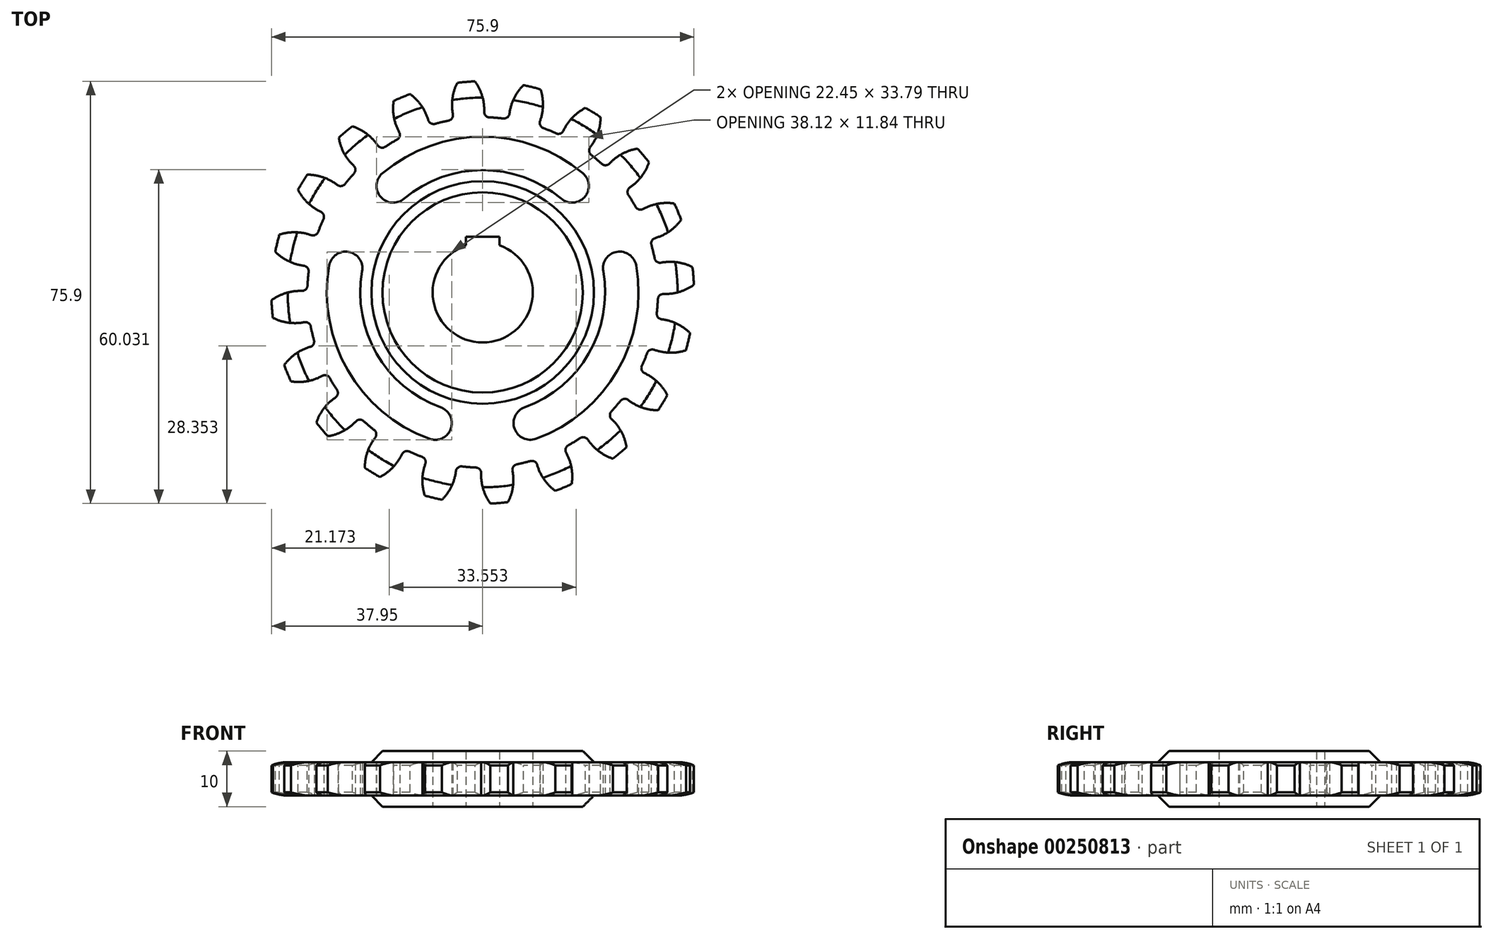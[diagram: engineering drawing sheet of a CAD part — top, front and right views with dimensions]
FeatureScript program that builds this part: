
annotation { "Feature Type Name" : "Feature", "Feature Type Description" : "" }
export const myFeature = defineFeature(function(context is Context, id is Id, definition is map)
    precondition{}
    {
        {
            var Q0;
            Q0=qCreatedBy(makeId("Top.planeOp"),FACE);
            var sketch = newSketch(context, id + "F0", { "sketchPlane" : qUnion([Q0])});
            skArc(sketch, "E0", {"start": v(-3, 8.49) * mm, "mid": v(0, -9) * mm, "end": v(3, 8.49) * mm});
            skCircle(sketch, "E1", {"center": v(0, 0) * mm, "radius": 25 * mm, "construction": true});
            skPoint(sketch, "E2", {"position": v(-46.68, 29.9) * mm});
            skArc(sketch, "E3", {"start": v(-21.67, 3.82) * mm, "mid": v(-24.1, 7.3) * mm, "end": v(-27.57, 4.86) * mm});
            skLineSegment(sketch, "E4", {"start": v(0, 0) * mm, "end": v(-24.62, 4.34) * mm, "construction": true});
            skArc(sketch, "E5", {"start": v(-9.58, -26.31) * mm, "mid": v(-5.73, -24.52) * mm, "end": v(-7.52, -20.67) * mm});
            skLineSegment(sketch, "E6", {"start": v(-8.55, -23.5) * mm, "end": v(0, 0) * mm, "construction": true});
            skArc(sketch, "E7", {"start": v(-27.57, 4.86) * mm, "mid": v(-24.25, -14) * mm, "end": v(-9.58, -26.31) * mm});
            skArc(sketch, "E8", {"start": v(-21.67, 3.82) * mm, "mid": v(-19.05, -11) * mm, "end": v(-7.52, -20.67) * mm});
            skArc(sketch, "E9.1.0", {"start": v(7.52, -20.67) * mm, "mid": v(19.05, -11) * mm, "end": v(21.67, 3.82) * mm});
            skArc(sketch, "E9.1.1", {"start": v(7.52, -20.67) * mm, "mid": v(5.73, -24.52) * mm, "end": v(9.58, -26.31) * mm});
            skArc(sketch, "E9.1.2", {"start": v(9.58, -26.31) * mm, "mid": v(24.25, -14) * mm, "end": v(27.57, 4.86) * mm});
            skArc(sketch, "E9.1.3", {"start": v(27.57, 4.86) * mm, "mid": v(24.1, 7.3) * mm, "end": v(21.67, 3.82) * mm});
            skArc(sketch, "E9.2.0", {"start": v(14.14, 16.85) * mm, "mid": v(0, 22) * mm, "end": v(-14.14, 16.85) * mm});
            skArc(sketch, "E9.2.1", {"start": v(14.14, 16.85) * mm, "mid": v(18.37, 17.22) * mm, "end": v(18, 21.45) * mm});
            skArc(sketch, "E9.2.2", {"start": v(18, 21.45) * mm, "mid": v(0, 28) * mm, "end": v(-18, 21.45) * mm});
            skLineSegment(sketch, "E10", {"start": v(-3, 8.49) * mm, "end": v(-3, 10) * mm});
            skLineSegment(sketch, "E11", {"start": v(-3, 10) * mm, "end": v(3, 10) * mm});
            skLineSegment(sketch, "E12", {"start": v(3, 10) * mm, "end": v(3, 8.49) * mm});
            skArc(sketch, "E13", {"start": v(-18, 21.45) * mm, "mid": v(-18.37, 17.22) * mm, "end": v(-14.14, 16.85) * mm});
            skArc(sketch, "E14", {"start": v(-1.4, 37.97) * mm, "mid": v(-2.98, 37.88) * mm, "end": v(-4.55, 37.73) * mm});
            skArc(sketch, "E15", {"start": v(-28.6, 13.2) * mm, "mid": v(-29.1, 12.05) * mm, "end": v(-29.55, 10.9) * mm});
            skLineSegment(sketch, "E16", {"start": v(0, 0) * mm, "end": v(0, 47.52) * mm, "construction": true});
            skArc(sketch, "E17", {"start": v(0.27, 32.5) * mm, "mid": v(-0.1, 35.38) * mm, "end": v(-1.4, 37.97) * mm});
            skLineSegment(sketch, "E18", {"start": v(0, 0) * mm, "end": v(-2.98, 37.88) * mm, "construction": true});
            skArc(sketch, "E19.MirrorCS", {"start": v(-5.36, 32.07) * mm, "mid": v(-5.43, 34.96) * mm, "end": v(-4.55, 37.73) * mm});
            skArc(sketch, "E20", {"start": v(-5.48, 34.57) * mm, "mid": v(2.75, -34.9) * mm, "end": v(0, 35) * mm, "construction": true});
            skArc(sketch, "E21", {"start": v(0, 35) * mm, "mid": v(-2.75, 34.9) * mm, "end": v(-5.48, 34.57) * mm, "construction": true});
            skArc(sketch, "E22", {"start": v(-6.14, 30.9) * mm, "mid": v(-5.5, 31.32) * mm, "end": v(-5.36, 32.07) * mm});
            skPoint(sketch, "E23.orphan", {"position": v(-5.1, 31.08) * mm});
            skArc(sketch, "E24.MirrorCS", {"start": v(1.23, 31.48) * mm, "mid": v(0.54, 31.8) * mm, "end": v(0.27, 32.5) * mm});
            skPoint(sketch, "E25.orphan", {"position": v(0.18, 31.5) * mm});
            skArc(sketch, "E26.1.0", {"start": v(3.7, 31.28) * mm, "mid": v(4.44, 31.49) * mm, "end": v(4.82, 32.15) * mm});
            skArc(sketch, "E26.1.1", {"start": v(4.82, 32.15) * mm, "mid": v(5.64, 34.93) * mm, "end": v(7.33, 37.29) * mm});
            skArc(sketch, "E26.1.2", {"start": v(10.4, 36.55) * mm, "mid": v(8.87, 36.95) * mm, "end": v(7.33, 37.29) * mm});
            skArc(sketch, "E26.1.3", {"start": v(10.3, 30.83) * mm, "mid": v(10.83, 33.68) * mm, "end": v(10.4, 36.55) * mm});
            skArc(sketch, "E26.1.4", {"start": v(10.9, 29.55) * mm, "mid": v(10.34, 30.07) * mm, "end": v(10.3, 30.83) * mm});
            skArc(sketch, "E26.2.0", {"start": v(13.2, 28.6) * mm, "mid": v(13.95, 28.57) * mm, "end": v(14.51, 29.1) * mm});
            skArc(sketch, "E26.2.1", {"start": v(14.51, 29.1) * mm, "mid": v(16.16, 31.48) * mm, "end": v(18.5, 33.2) * mm});
            skArc(sketch, "E26.2.2", {"start": v(21.18, 31.55) * mm, "mid": v(19.86, 32.4) * mm, "end": v(18.5, 33.2) * mm});
            skArc(sketch, "E26.2.3", {"start": v(19.33, 26.14) * mm, "mid": v(20.7, 28.69) * mm, "end": v(21.18, 31.55) * mm});
            skArc(sketch, "E26.2.4", {"start": v(19.5, 24.74) * mm, "mid": v(19.13, 25.4) * mm, "end": v(19.33, 26.14) * mm});
            skArc(sketch, "E26.3.0", {"start": v(21.38, 23.13) * mm, "mid": v(22.1, 22.86) * mm, "end": v(22.8, 23.18) * mm});
            skArc(sketch, "E26.3.1", {"start": v(22.8, 23.18) * mm, "mid": v(25.1, 24.94) * mm, "end": v(27.85, 25.86) * mm});
            skArc(sketch, "E26.3.2", {"start": v(29.9, 23.46) * mm, "mid": v(28.9, 24.68) * mm, "end": v(27.85, 25.86) * mm});
            skArc(sketch, "E26.3.3", {"start": v(26.46, 18.89) * mm, "mid": v(28.56, 20.89) * mm, "end": v(29.9, 23.46) * mm});
            skArc(sketch, "E26.3.4", {"start": v(26.19, 17.5) * mm, "mid": v(26.04, 18.25) * mm, "end": v(26.46, 18.89) * mm});
            skArc(sketch, "E26.4.0", {"start": v(27.48, 15.39) * mm, "mid": v(28.08, 14.92) * mm, "end": v(28.84, 15) * mm});
            skArc(sketch, "E26.4.1", {"start": v(28.84, 15) * mm, "mid": v(31.58, 15.97) * mm, "end": v(34.47, 15.98) * mm});
            skArc(sketch, "E26.4.2", {"start": v(35.68, 13.07) * mm, "mid": v(35.1, 14.54) * mm, "end": v(34.47, 15.98) * mm});
            skArc(sketch, "E26.4.3", {"start": v(31, 9.79) * mm, "mid": v(33.62, 11.04) * mm, "end": v(35.68, 13.07) * mm});
            skArc(sketch, "E26.4.4", {"start": v(30.32, 8.55) * mm, "mid": v(30.4, 9.31) * mm, "end": v(31, 9.79) * mm});
            skArc(sketch, "E26.5.0", {"start": v(30.9, 6.14) * mm, "mid": v(31.32, 5.5) * mm, "end": v(32.07, 5.36) * mm});
            skArc(sketch, "E26.5.1", {"start": v(32.07, 5.36) * mm, "mid": v(34.96, 5.43) * mm, "end": v(37.73, 4.55) * mm});
            skArc(sketch, "E26.5.2", {"start": v(37.97, 1.4) * mm, "mid": v(37.88, 2.98) * mm, "end": v(37.73, 4.55) * mm});
            skArc(sketch, "E26.5.3", {"start": v(32.5, -0.27) * mm, "mid": v(35.38, 0.1) * mm, "end": v(37.97, 1.4) * mm});
            skArc(sketch, "E26.5.4", {"start": v(31.48, -1.23) * mm, "mid": v(31.8, -0.54) * mm, "end": v(32.5, -0.27) * mm});
            skArc(sketch, "E26.6.0", {"start": v(31.28, -3.7) * mm, "mid": v(31.49, -4.44) * mm, "end": v(32.15, -4.82) * mm});
            skArc(sketch, "E26.6.1", {"start": v(32.15, -4.82) * mm, "mid": v(34.93, -5.64) * mm, "end": v(37.29, -7.33) * mm});
            skArc(sketch, "E26.6.2", {"start": v(36.55, -10.4) * mm, "mid": v(36.95, -8.87) * mm, "end": v(37.29, -7.33) * mm});
            skArc(sketch, "E26.6.3", {"start": v(30.83, -10.3) * mm, "mid": v(33.68, -10.83) * mm, "end": v(36.55, -10.4) * mm});
            skArc(sketch, "E26.6.4", {"start": v(29.55, -10.9) * mm, "mid": v(30.07, -10.34) * mm, "end": v(30.83, -10.3) * mm});
            skArc(sketch, "E26.7.0", {"start": v(28.6, -13.2) * mm, "mid": v(28.57, -13.95) * mm, "end": v(29.1, -14.51) * mm});
            skArc(sketch, "E26.7.1", {"start": v(29.1, -14.51) * mm, "mid": v(31.48, -16.16) * mm, "end": v(33.2, -18.5) * mm});
            skArc(sketch, "E26.7.2", {"start": v(31.55, -21.18) * mm, "mid": v(32.4, -19.86) * mm, "end": v(33.2, -18.5) * mm});
            skArc(sketch, "E26.7.3", {"start": v(26.14, -19.33) * mm, "mid": v(28.69, -20.7) * mm, "end": v(31.55, -21.18) * mm});
            skArc(sketch, "E26.7.4", {"start": v(24.74, -19.5) * mm, "mid": v(25.4, -19.13) * mm, "end": v(26.14, -19.33) * mm});
            skArc(sketch, "E26.8.0", {"start": v(23.13, -21.38) * mm, "mid": v(22.86, -22.1) * mm, "end": v(23.18, -22.8) * mm});
            skArc(sketch, "E26.8.1", {"start": v(23.18, -22.8) * mm, "mid": v(24.94, -25.1) * mm, "end": v(25.86, -27.85) * mm});
            skArc(sketch, "E26.8.2", {"start": v(23.46, -29.9) * mm, "mid": v(24.68, -28.9) * mm, "end": v(25.86, -27.85) * mm});
            skArc(sketch, "E26.8.3", {"start": v(18.89, -26.46) * mm, "mid": v(20.89, -28.56) * mm, "end": v(23.46, -29.9) * mm});
            skArc(sketch, "E26.8.4", {"start": v(17.5, -26.19) * mm, "mid": v(18.25, -26.04) * mm, "end": v(18.89, -26.46) * mm});
            skArc(sketch, "E26.9.0", {"start": v(15.39, -27.48) * mm, "mid": v(14.92, -28.08) * mm, "end": v(15, -28.84) * mm});
            skArc(sketch, "E26.9.1", {"start": v(15, -28.84) * mm, "mid": v(15.97, -31.58) * mm, "end": v(15.98, -34.47) * mm});
            skArc(sketch, "E26.9.2", {"start": v(13.07, -35.68) * mm, "mid": v(14.54, -35.1) * mm, "end": v(15.98, -34.47) * mm});
            skArc(sketch, "E26.9.3", {"start": v(9.79, -31) * mm, "mid": v(11.04, -33.62) * mm, "end": v(13.07, -35.68) * mm});
            skArc(sketch, "E26.9.4", {"start": v(8.55, -30.32) * mm, "mid": v(9.31, -30.4) * mm, "end": v(9.79, -31) * mm});
            skArc(sketch, "E26.10.0", {"start": v(6.14, -30.9) * mm, "mid": v(5.5, -31.32) * mm, "end": v(5.36, -32.07) * mm});
            skArc(sketch, "E26.10.1", {"start": v(5.36, -32.07) * mm, "mid": v(5.43, -34.96) * mm, "end": v(4.55, -37.73) * mm});
            skArc(sketch, "E26.10.2", {"start": v(1.4, -37.97) * mm, "mid": v(2.98, -37.88) * mm, "end": v(4.55, -37.73) * mm});
            skArc(sketch, "E26.10.3", {"start": v(-0.27, -32.5) * mm, "mid": v(0.1, -35.38) * mm, "end": v(1.4, -37.97) * mm});
            skArc(sketch, "E26.10.4", {"start": v(-1.23, -31.48) * mm, "mid": v(-0.54, -31.8) * mm, "end": v(-0.27, -32.5) * mm});
            skArc(sketch, "E26.11.0", {"start": v(-3.7, -31.28) * mm, "mid": v(-4.44, -31.49) * mm, "end": v(-4.82, -32.15) * mm});
            skArc(sketch, "E26.11.1", {"start": v(-4.82, -32.15) * mm, "mid": v(-5.64, -34.93) * mm, "end": v(-7.33, -37.29) * mm});
            skArc(sketch, "E26.11.2", {"start": v(-10.4, -36.55) * mm, "mid": v(-8.87, -36.95) * mm, "end": v(-7.33, -37.29) * mm});
            skArc(sketch, "E26.11.3", {"start": v(-10.3, -30.83) * mm, "mid": v(-10.83, -33.68) * mm, "end": v(-10.4, -36.55) * mm});
            skArc(sketch, "E26.11.4", {"start": v(-10.9, -29.55) * mm, "mid": v(-10.34, -30.07) * mm, "end": v(-10.3, -30.83) * mm});
            skArc(sketch, "E26.12.0", {"start": v(-13.2, -28.6) * mm, "mid": v(-13.95, -28.57) * mm, "end": v(-14.51, -29.1) * mm});
            skArc(sketch, "E26.12.1", {"start": v(-14.51, -29.1) * mm, "mid": v(-16.16, -31.48) * mm, "end": v(-18.5, -33.2) * mm});
            skArc(sketch, "E26.12.2", {"start": v(-21.18, -31.55) * mm, "mid": v(-19.86, -32.4) * mm, "end": v(-18.5, -33.2) * mm});
            skArc(sketch, "E26.12.3", {"start": v(-19.33, -26.14) * mm, "mid": v(-20.7, -28.69) * mm, "end": v(-21.18, -31.55) * mm});
            skArc(sketch, "E26.12.4", {"start": v(-19.5, -24.74) * mm, "mid": v(-19.13, -25.4) * mm, "end": v(-19.33, -26.14) * mm});
            skArc(sketch, "E26.13.0", {"start": v(-21.38, -23.13) * mm, "mid": v(-22.1, -22.86) * mm, "end": v(-22.8, -23.18) * mm});
            skArc(sketch, "E26.13.1", {"start": v(-22.8, -23.18) * mm, "mid": v(-25.1, -24.94) * mm, "end": v(-27.85, -25.86) * mm});
            skArc(sketch, "E26.13.2", {"start": v(-29.9, -23.46) * mm, "mid": v(-28.9, -24.68) * mm, "end": v(-27.85, -25.86) * mm});
            skArc(sketch, "E26.13.3", {"start": v(-26.46, -18.89) * mm, "mid": v(-28.56, -20.89) * mm, "end": v(-29.9, -23.46) * mm});
            skArc(sketch, "E26.13.4", {"start": v(-26.19, -17.5) * mm, "mid": v(-26.04, -18.25) * mm, "end": v(-26.46, -18.89) * mm});
            skArc(sketch, "E26.14.0", {"start": v(-27.48, -15.39) * mm, "mid": v(-28.08, -14.92) * mm, "end": v(-28.84, -15) * mm});
            skArc(sketch, "E26.14.1", {"start": v(-28.84, -15) * mm, "mid": v(-31.58, -15.97) * mm, "end": v(-34.47, -15.98) * mm});
            skArc(sketch, "E26.14.2", {"start": v(-35.68, -13.07) * mm, "mid": v(-35.1, -14.54) * mm, "end": v(-34.47, -15.98) * mm});
            skArc(sketch, "E26.14.3", {"start": v(-31, -9.79) * mm, "mid": v(-33.62, -11.04) * mm, "end": v(-35.68, -13.07) * mm});
            skArc(sketch, "E26.14.4", {"start": v(-30.32, -8.55) * mm, "mid": v(-30.4, -9.31) * mm, "end": v(-31, -9.79) * mm});
            skArc(sketch, "E26.15.0", {"start": v(-30.9, -6.14) * mm, "mid": v(-31.32, -5.5) * mm, "end": v(-32.07, -5.36) * mm});
            skArc(sketch, "E26.15.1", {"start": v(-32.07, -5.36) * mm, "mid": v(-34.96, -5.43) * mm, "end": v(-37.73, -4.55) * mm});
            skArc(sketch, "E26.15.2", {"start": v(-37.97, -1.4) * mm, "mid": v(-37.88, -2.98) * mm, "end": v(-37.73, -4.55) * mm});
            skArc(sketch, "E26.15.3", {"start": v(-32.5, 0.27) * mm, "mid": v(-35.38, -0.1) * mm, "end": v(-37.97, -1.4) * mm});
            skArc(sketch, "E26.15.4", {"start": v(-31.48, 1.23) * mm, "mid": v(-31.8, 0.54) * mm, "end": v(-32.5, 0.27) * mm});
            skArc(sketch, "E26.16.0", {"start": v(-31.28, 3.7) * mm, "mid": v(-31.49, 4.44) * mm, "end": v(-32.15, 4.82) * mm});
            skArc(sketch, "E26.16.1", {"start": v(-32.15, 4.82) * mm, "mid": v(-34.93, 5.64) * mm, "end": v(-37.29, 7.33) * mm});
            skArc(sketch, "E26.16.2", {"start": v(-36.55, 10.4) * mm, "mid": v(-36.95, 8.87) * mm, "end": v(-37.29, 7.33) * mm});
            skArc(sketch, "E26.16.3", {"start": v(-30.83, 10.3) * mm, "mid": v(-33.68, 10.83) * mm, "end": v(-36.55, 10.4) * mm});
            skArc(sketch, "E26.16.4", {"start": v(-29.55, 10.9) * mm, "mid": v(-30.07, 10.34) * mm, "end": v(-30.83, 10.3) * mm});
            skArc(sketch, "E26.17.0", {"start": v(-28.6, 13.2) * mm, "mid": v(-28.57, 13.95) * mm, "end": v(-29.1, 14.51) * mm});
            skArc(sketch, "E26.17.1", {"start": v(-29.1, 14.51) * mm, "mid": v(-31.48, 16.16) * mm, "end": v(-33.2, 18.5) * mm});
            skArc(sketch, "E26.17.2", {"start": v(-31.55, 21.18) * mm, "mid": v(-32.4, 19.86) * mm, "end": v(-33.2, 18.5) * mm});
            skArc(sketch, "E26.17.3", {"start": v(-26.14, 19.33) * mm, "mid": v(-28.69, 20.7) * mm, "end": v(-31.55, 21.18) * mm});
            skArc(sketch, "E26.17.4", {"start": v(-24.74, 19.5) * mm, "mid": v(-25.4, 19.13) * mm, "end": v(-26.14, 19.33) * mm});
            skArc(sketch, "E26.18.0", {"start": v(-23.13, 21.38) * mm, "mid": v(-22.86, 22.1) * mm, "end": v(-23.18, 22.8) * mm});
            skArc(sketch, "E26.18.1", {"start": v(-23.18, 22.8) * mm, "mid": v(-24.94, 25.1) * mm, "end": v(-25.86, 27.85) * mm});
            skArc(sketch, "E26.18.2", {"start": v(-23.46, 29.9) * mm, "mid": v(-24.68, 28.9) * mm, "end": v(-25.86, 27.85) * mm});
            skArc(sketch, "E26.18.3", {"start": v(-18.89, 26.46) * mm, "mid": v(-20.89, 28.56) * mm, "end": v(-23.46, 29.9) * mm});
            skArc(sketch, "E26.18.4", {"start": v(-17.5, 26.19) * mm, "mid": v(-18.25, 26.04) * mm, "end": v(-18.89, 26.46) * mm});
            skArc(sketch, "E26.19.0", {"start": v(-15.39, 27.48) * mm, "mid": v(-14.92, 28.08) * mm, "end": v(-15, 28.84) * mm});
            skArc(sketch, "E26.19.1", {"start": v(-15, 28.84) * mm, "mid": v(-15.97, 31.58) * mm, "end": v(-15.98, 34.47) * mm});
            skArc(sketch, "E26.19.2", {"start": v(-13.07, 35.68) * mm, "mid": v(-14.54, 35.1) * mm, "end": v(-15.98, 34.47) * mm});
            skArc(sketch, "E26.19.3", {"start": v(-9.79, 31) * mm, "mid": v(-11.04, 33.62) * mm, "end": v(-13.07, 35.68) * mm});
            skArc(sketch, "E26.19.4", {"start": v(-8.55, 30.32) * mm, "mid": v(-9.31, 30.4) * mm, "end": v(-9.79, 31) * mm});
            skLineSegment(sketch, "E26.anchor1", {"start": v(0, 0) * mm, "end": v(-6.14, 30.9) * mm, "construction": true});
            skLineSegment(sketch, "E26.anchor2", {"start": v(0, 0) * mm, "end": v(-15.39, 27.48) * mm, "construction": true});
            skArc(sketch, "E27.trimOffspring", {"start": v(-23.13, 21.38) * mm, "mid": v(-23.95, 20.46) * mm, "end": v(-24.74, 19.5) * mm});
            skArc(sketch, "E28.trimOffspring", {"start": v(-15.39, 27.48) * mm, "mid": v(-16.46, 26.86) * mm, "end": v(-17.5, 26.19) * mm});
            skArc(sketch, "E29.trimOffspring", {"start": v(-6.14, 30.9) * mm, "mid": v(-7.35, 30.63) * mm, "end": v(-8.55, 30.32) * mm});
            skArc(sketch, "E30.trimOffspring", {"start": v(3.7, 31.28) * mm, "mid": v(2.47, 31.4) * mm, "end": v(1.23, 31.48) * mm});
            skArc(sketch, "E31.trimOffspring", {"start": v(13.2, 28.6) * mm, "mid": v(12.05, 29.1) * mm, "end": v(10.9, 29.55) * mm});
            skArc(sketch, "E32.trimOffspring", {"start": v(21.38, 23.13) * mm, "mid": v(20.46, 23.95) * mm, "end": v(19.5, 24.74) * mm});
            skArc(sketch, "E33.trimOffspring", {"start": v(27.48, 15.39) * mm, "mid": v(26.86, 16.46) * mm, "end": v(26.19, 17.5) * mm});
            skArc(sketch, "E34.trimOffspring", {"start": v(30.9, 6.14) * mm, "mid": v(30.63, 7.35) * mm, "end": v(30.32, 8.55) * mm});
            skArc(sketch, "E35.trimOffspring", {"start": v(31.28, -3.7) * mm, "mid": v(31.4, -2.47) * mm, "end": v(31.48, -1.23) * mm});
            skArc(sketch, "E36.trimOffspring", {"start": v(28.6, -13.2) * mm, "mid": v(29.1, -12.05) * mm, "end": v(29.55, -10.9) * mm});
            skArc(sketch, "E37.trimOffspring", {"start": v(23.13, -21.38) * mm, "mid": v(23.95, -20.46) * mm, "end": v(24.74, -19.5) * mm});
            skArc(sketch, "E38.trimOffspring", {"start": v(15.39, -27.48) * mm, "mid": v(16.46, -26.86) * mm, "end": v(17.5, -26.19) * mm});
            skArc(sketch, "E39.trimOffspring", {"start": v(6.14, -30.9) * mm, "mid": v(7.35, -30.63) * mm, "end": v(8.55, -30.32) * mm});
            skArc(sketch, "E40.trimOffspring", {"start": v(-3.7, -31.28) * mm, "mid": v(-2.47, -31.4) * mm, "end": v(-1.23, -31.48) * mm});
            skArc(sketch, "E41.trimOffspring", {"start": v(-13.2, -28.6) * mm, "mid": v(-12.05, -29.1) * mm, "end": v(-10.9, -29.55) * mm});
            skArc(sketch, "E42.trimOffspring", {"start": v(-21.38, -23.13) * mm, "mid": v(-20.46, -23.95) * mm, "end": v(-19.5, -24.74) * mm});
            skArc(sketch, "E43.trimOffspring", {"start": v(-27.48, -15.39) * mm, "mid": v(-26.86, -16.46) * mm, "end": v(-26.19, -17.5) * mm});
            skArc(sketch, "E44.trimOffspring", {"start": v(-30.9, -6.14) * mm, "mid": v(-30.63, -7.35) * mm, "end": v(-30.32, -8.55) * mm});
            skArc(sketch, "E45.trimOffspring", {"start": v(-31.28, 3.7) * mm, "mid": v(-31.4, 2.47) * mm, "end": v(-31.48, 1.23) * mm});
            skSolve(sketch);
        }
        {
            var Q0;
            Q0=makeQuery(id+"F0.imprint","IMPRINT",FACE,{"disambiguationData":[TD([[makeQuery(id+"F0.imprint","IMPRINT",EDGE,{"derivedFrom":sQuery(id+"F0.wireOp",EDGE,"E0")}),-1.0]])]});
            extrude(context, id + "F1", {"entities" : qUnion([Q0]), "depth" : 6 * mm, "offsetDistance" : 25 * mm, "symmetric" : true});
        }
        {
            var Q0;
            Q0=qCreatedBy(makeId("Right.planeOp"),FACE);
            var sketch = newSketch(context, id + "F2", { "sketchPlane" : qUnion([Q0])});
            skLineSegment(sketch, "E46", {"start": v(37.97, 2.44) * mm, "end": v(37.97, -2.43) * mm});
            skLineSegment(sketch, "E47", {"start": v(34.73, 3) * mm, "end": v(34.73, -9.64) * mm, "construction": true});
            skArc(sketch, "E48", {"start": v(37.97, 2.44) * mm, "mid": v(36.38, 2.87) * mm, "end": v(34.73, 3) * mm});
            skArc(sketch, "E49.MirrorCS", {"start": v(37.97, -2.44) * mm, "mid": v(36.38, -2.87) * mm, "end": v(34.73, -3) * mm});
            skLineSegment(sketch, "E50", {"start": v(34.73, 3) * mm, "end": v(34.73, 3.33) * mm});
            skLineSegment(sketch, "E51", {"start": v(34.73, 3.33) * mm, "end": v(39.08, 3.33) * mm});
            skLineSegment(sketch, "E52", {"start": v(39.08, 3.33) * mm, "end": v(39.08, -3.22) * mm});
            skLineSegment(sketch, "E53", {"start": v(39.08, -3.22) * mm, "end": v(34.73, -3.32) * mm});
            skLineSegment(sketch, "E54", {"start": v(34.73, -3.32) * mm, "end": v(34.73, -3) * mm});
            skSolve(sketch);
        }
        {
            var Q0;
            Q0=makeQuery(id+"F2.imprint","IMPRINT",FACE,{"disambiguationData":[TD([[makeQuery(id+"F2.imprint","IMPRINT",EDGE,{"derivedFrom":sQuery(id+"F2.wireOp",EDGE,"E46")}),1.0]])]});
            var Q1;
            Q1=makeQuery(id+"F1.opExtrude","SWEPT_FACE",FACE,{"disambiguationData":[OSD([sQuery(id+"F0.wireOp",EDGE,"E0")])]});
            revolve(context, id + "F3", {"operationType" : NewBodyOperationType.REMOVE, "surfaceOperationType" : NewSurfaceOperationType.NEW, "entities" : qUnion([Q0]), "axis" : qUnion([Q1]), "revolveType" : RevolveType.FULL, "oppositeDirection" : true});
        }
        {
            var Q0;
            Q0=qCreatedBy(makeId("Top.planeOp"),FACE);
            var sketch = newSketch(context, id + "F4", { "sketchPlane" : qUnion([Q0])});
            skCircle(sketch, "E55", {"center": v(0, 0) * mm, "radius": 18 * mm});
            skArc(sketch, "E56", {"start": v(-3, 8.49) * mm, "mid": v(0, -9) * mm, "end": v(3, 8.49) * mm});
            skLineSegment(sketch, "E57", {"start": v(3, 8.49) * mm, "end": v(3, 10) * mm});
            skLineSegment(sketch, "E58", {"start": v(3, 10) * mm, "end": v(-3, 10) * mm});
            skLineSegment(sketch, "E59", {"start": v(-3, 10) * mm, "end": v(-3, 8.49) * mm});
            skSolve(sketch);
        }
        {
            var Q0;
            Q0 = qSketchRegion(id + "F4", true);
            extrude(context, id + "F5", {"entities" : qUnion([Q0]), "operationType" : NewBodyOperationType.ADD, "depth" : 10 * mm, "offsetDistance" : 25 * mm, "symmetric" : true});
        }
        {
            var Q0;
            Q0=makeQuery(id+"F5.boolean.opBoolean","INTERSECT",EDGE,{"derivedFrom":[makeQuery(id+"F1.opExtrude","CAP_FACE",FACE,{"disambiguationData":[OSD([sQuery(id+"F0.wireOp",EDGE,"E0"),sQuery(id+"F0.wireOp",EDGE,"E3"),sQuery(id+"F0.wireOp",EDGE,"E5"),sQuery(id+"F0.wireOp",EDGE,"E7"),sQuery(id+"F0.wireOp",EDGE,"E8"),sQuery(id+"F0.wireOp",EDGE,"E9.1.0"),sQuery(id+"F0.wireOp",EDGE,"E9.1.1"),sQuery(id+"F0.wireOp",EDGE,"E9.1.2"),sQuery(id+"F0.wireOp",EDGE,"E9.1.3"),sQuery(id+"F0.wireOp",EDGE,"E9.2.0"),sQuery(id+"F0.wireOp",EDGE,"E9.2.1"),sQuery(id+"F0.wireOp",EDGE,"E9.2.2"),sQuery(id+"F0.wireOp",EDGE,"E10"),sQuery(id+"F0.wireOp",EDGE,"E11"),sQuery(id+"F0.wireOp",EDGE,"E12"),sQuery(id+"F0.wireOp",EDGE,"E13"),sQuery(id+"F0.wireOp",EDGE,"E14"),sQuery(id+"F0.wireOp",EDGE,"E15"),sQuery(id+"F0.wireOp",EDGE,"E17"),sQuery(id+"F0.wireOp",EDGE,"E19.MirrorCS"),sQuery(id+"F0.wireOp",EDGE,"E22"),sQuery(id+"F0.wireOp",EDGE,"E24.MirrorCS"),sQuery(id+"F0.wireOp",EDGE,"E26.1.0"),sQuery(id+"F0.wireOp",EDGE,"E26.1.1"),sQuery(id+"F0.wireOp",EDGE,"E26.1.2"),sQuery(id+"F0.wireOp",EDGE,"E26.1.3"),sQuery(id+"F0.wireOp",EDGE,"E26.1.4"),sQuery(id+"F0.wireOp",EDGE,"E26.2.0"),sQuery(id+"F0.wireOp",EDGE,"E26.2.1"),sQuery(id+"F0.wireOp",EDGE,"E26.2.2"),sQuery(id+"F0.wireOp",EDGE,"E26.2.3"),sQuery(id+"F0.wireOp",EDGE,"E26.2.4"),sQuery(id+"F0.wireOp",EDGE,"E26.3.0"),sQuery(id+"F0.wireOp",EDGE,"E26.3.1"),sQuery(id+"F0.wireOp",EDGE,"E26.3.2"),sQuery(id+"F0.wireOp",EDGE,"E26.3.3"),sQuery(id+"F0.wireOp",EDGE,"E26.3.4"),sQuery(id+"F0.wireOp",EDGE,"E26.4.0"),sQuery(id+"F0.wireOp",EDGE,"E26.4.1"),sQuery(id+"F0.wireOp",EDGE,"E26.4.2"),sQuery(id+"F0.wireOp",EDGE,"E26.4.3"),sQuery(id+"F0.wireOp",EDGE,"E26.4.4"),sQuery(id+"F0.wireOp",EDGE,"E26.5.0"),sQuery(id+"F0.wireOp",EDGE,"E26.5.1"),sQuery(id+"F0.wireOp",EDGE,"E26.5.2"),sQuery(id+"F0.wireOp",EDGE,"E26.5.3"),sQuery(id+"F0.wireOp",EDGE,"E26.5.4"),sQuery(id+"F0.wireOp",EDGE,"E26.6.0"),sQuery(id+"F0.wireOp",EDGE,"E26.6.1"),sQuery(id+"F0.wireOp",EDGE,"E26.6.2"),sQuery(id+"F0.wireOp",EDGE,"E26.6.3"),sQuery(id+"F0.wireOp",EDGE,"E26.6.4"),sQuery(id+"F0.wireOp",EDGE,"E26.7.0"),sQuery(id+"F0.wireOp",EDGE,"E26.7.1"),sQuery(id+"F0.wireOp",EDGE,"E26.7.2"),sQuery(id+"F0.wireOp",EDGE,"E26.7.3"),sQuery(id+"F0.wireOp",EDGE,"E26.7.4"),sQuery(id+"F0.wireOp",EDGE,"E26.8.0"),sQuery(id+"F0.wireOp",EDGE,"E26.8.1"),sQuery(id+"F0.wireOp",EDGE,"E26.8.2"),sQuery(id+"F0.wireOp",EDGE,"E26.8.3"),sQuery(id+"F0.wireOp",EDGE,"E26.8.4"),sQuery(id+"F0.wireOp",EDGE,"E26.9.0"),sQuery(id+"F0.wireOp",EDGE,"E26.9.1"),sQuery(id+"F0.wireOp",EDGE,"E26.9.2"),sQuery(id+"F0.wireOp",EDGE,"E26.9.3"),sQuery(id+"F0.wireOp",EDGE,"E26.9.4"),sQuery(id+"F0.wireOp",EDGE,"E26.10.0"),sQuery(id+"F0.wireOp",EDGE,"E26.10.1"),sQuery(id+"F0.wireOp",EDGE,"E26.10.2"),sQuery(id+"F0.wireOp",EDGE,"E26.10.3"),sQuery(id+"F0.wireOp",EDGE,"E26.10.4"),sQuery(id+"F0.wireOp",EDGE,"E26.11.0"),sQuery(id+"F0.wireOp",EDGE,"E26.11.1"),sQuery(id+"F0.wireOp",EDGE,"E26.11.2"),sQuery(id+"F0.wireOp",EDGE,"E26.11.3"),sQuery(id+"F0.wireOp",EDGE,"E26.11.4"),sQuery(id+"F0.wireOp",EDGE,"E26.12.0"),sQuery(id+"F0.wireOp",EDGE,"E26.12.1"),sQuery(id+"F0.wireOp",EDGE,"E26.12.2"),sQuery(id+"F0.wireOp",EDGE,"E26.12.3"),sQuery(id+"F0.wireOp",EDGE,"E26.12.4"),sQuery(id+"F0.wireOp",EDGE,"E26.13.0"),sQuery(id+"F0.wireOp",EDGE,"E26.13.1"),sQuery(id+"F0.wireOp",EDGE,"E26.13.2"),sQuery(id+"F0.wireOp",EDGE,"E26.13.3"),sQuery(id+"F0.wireOp",EDGE,"E26.13.4"),sQuery(id+"F0.wireOp",EDGE,"E26.14.0"),sQuery(id+"F0.wireOp",EDGE,"E26.14.1"),sQuery(id+"F0.wireOp",EDGE,"E26.14.2"),sQuery(id+"F0.wireOp",EDGE,"E26.14.3"),sQuery(id+"F0.wireOp",EDGE,"E26.14.4"),sQuery(id+"F0.wireOp",EDGE,"E26.15.0"),sQuery(id+"F0.wireOp",EDGE,"E26.15.1"),sQuery(id+"F0.wireOp",EDGE,"E26.15.2"),sQuery(id+"F0.wireOp",EDGE,"E26.15.3"),sQuery(id+"F0.wireOp",EDGE,"E26.15.4"),sQuery(id+"F0.wireOp",EDGE,"E26.16.0"),sQuery(id+"F0.wireOp",EDGE,"E26.16.1"),sQuery(id+"F0.wireOp",EDGE,"E26.16.2"),sQuery(id+"F0.wireOp",EDGE,"E26.16.3"),sQuery(id+"F0.wireOp",EDGE,"E26.16.4"),sQuery(id+"F0.wireOp",EDGE,"E26.17.0"),sQuery(id+"F0.wireOp",EDGE,"E26.17.1"),sQuery(id+"F0.wireOp",EDGE,"E26.17.2"),sQuery(id+"F0.wireOp",EDGE,"E26.17.3"),sQuery(id+"F0.wireOp",EDGE,"E26.17.4"),sQuery(id+"F0.wireOp",EDGE,"E26.18.0"),sQuery(id+"F0.wireOp",EDGE,"E26.18.1"),sQuery(id+"F0.wireOp",EDGE,"E26.18.2"),sQuery(id+"F0.wireOp",EDGE,"E26.18.3"),sQuery(id+"F0.wireOp",EDGE,"E26.18.4"),sQuery(id+"F0.wireOp",EDGE,"E26.19.0"),sQuery(id+"F0.wireOp",EDGE,"E26.19.1"),sQuery(id+"F0.wireOp",EDGE,"E26.19.2"),sQuery(id+"F0.wireOp",EDGE,"E26.19.3"),sQuery(id+"F0.wireOp",EDGE,"E26.19.4"),sQuery(id+"F0.wireOp",EDGE,"E27.trimOffspring"),sQuery(id+"F0.wireOp",EDGE,"E28.trimOffspring"),sQuery(id+"F0.wireOp",EDGE,"E29.trimOffspring"),sQuery(id+"F0.wireOp",EDGE,"E30.trimOffspring"),sQuery(id+"F0.wireOp",EDGE,"E31.trimOffspring"),sQuery(id+"F0.wireOp",EDGE,"E32.trimOffspring"),sQuery(id+"F0.wireOp",EDGE,"E33.trimOffspring"),sQuery(id+"F0.wireOp",EDGE,"E34.trimOffspring"),sQuery(id+"F0.wireOp",EDGE,"E35.trimOffspring"),sQuery(id+"F0.wireOp",EDGE,"E36.trimOffspring"),sQuery(id+"F0.wireOp",EDGE,"E37.trimOffspring"),sQuery(id+"F0.wireOp",EDGE,"E38.trimOffspring"),sQuery(id+"F0.wireOp",EDGE,"E39.trimOffspring"),sQuery(id+"F0.wireOp",EDGE,"E40.trimOffspring"),sQuery(id+"F0.wireOp",EDGE,"E41.trimOffspring"),sQuery(id+"F0.wireOp",EDGE,"E42.trimOffspring"),sQuery(id+"F0.wireOp",EDGE,"E43.trimOffspring"),sQuery(id+"F0.wireOp",EDGE,"E44.trimOffspring"),sQuery(id+"F0.wireOp",EDGE,"E45.trimOffspring")])],"isStart":false}),makeQuery(id+"F5.opExtrude","SWEPT_FACE",FACE,{"disambiguationData":[OSD([sQuery(id+"F4.wireOp",EDGE,"E55")])]})]});
            chamfer(context, id + "F6", {"entities" : qUnion([Q0]), "width" : 2 * mm, "tangentPropagation" : true});
        }
        {
            var Q0;
            Q0=makeQuery(id+"F5.boolean.opBoolean","INTERSECT",EDGE,{"derivedFrom":[makeQuery(id+"F1.opExtrude","CAP_FACE",FACE,{"disambiguationData":[OSD([sQuery(id+"F0.wireOp",EDGE,"E0"),sQuery(id+"F0.wireOp",EDGE,"E3"),sQuery(id+"F0.wireOp",EDGE,"E5"),sQuery(id+"F0.wireOp",EDGE,"E7"),sQuery(id+"F0.wireOp",EDGE,"E8"),sQuery(id+"F0.wireOp",EDGE,"E9.1.0"),sQuery(id+"F0.wireOp",EDGE,"E9.1.1"),sQuery(id+"F0.wireOp",EDGE,"E9.1.2"),sQuery(id+"F0.wireOp",EDGE,"E9.1.3"),sQuery(id+"F0.wireOp",EDGE,"E9.2.0"),sQuery(id+"F0.wireOp",EDGE,"E9.2.1"),sQuery(id+"F0.wireOp",EDGE,"E9.2.2"),sQuery(id+"F0.wireOp",EDGE,"E10"),sQuery(id+"F0.wireOp",EDGE,"E11"),sQuery(id+"F0.wireOp",EDGE,"E12"),sQuery(id+"F0.wireOp",EDGE,"E13"),sQuery(id+"F0.wireOp",EDGE,"E14"),sQuery(id+"F0.wireOp",EDGE,"E15"),sQuery(id+"F0.wireOp",EDGE,"E17"),sQuery(id+"F0.wireOp",EDGE,"E19.MirrorCS"),sQuery(id+"F0.wireOp",EDGE,"E22"),sQuery(id+"F0.wireOp",EDGE,"E24.MirrorCS"),sQuery(id+"F0.wireOp",EDGE,"E26.1.0"),sQuery(id+"F0.wireOp",EDGE,"E26.1.1"),sQuery(id+"F0.wireOp",EDGE,"E26.1.2"),sQuery(id+"F0.wireOp",EDGE,"E26.1.3"),sQuery(id+"F0.wireOp",EDGE,"E26.1.4"),sQuery(id+"F0.wireOp",EDGE,"E26.2.0"),sQuery(id+"F0.wireOp",EDGE,"E26.2.1"),sQuery(id+"F0.wireOp",EDGE,"E26.2.2"),sQuery(id+"F0.wireOp",EDGE,"E26.2.3"),sQuery(id+"F0.wireOp",EDGE,"E26.2.4"),sQuery(id+"F0.wireOp",EDGE,"E26.3.0"),sQuery(id+"F0.wireOp",EDGE,"E26.3.1"),sQuery(id+"F0.wireOp",EDGE,"E26.3.2"),sQuery(id+"F0.wireOp",EDGE,"E26.3.3"),sQuery(id+"F0.wireOp",EDGE,"E26.3.4"),sQuery(id+"F0.wireOp",EDGE,"E26.4.0"),sQuery(id+"F0.wireOp",EDGE,"E26.4.1"),sQuery(id+"F0.wireOp",EDGE,"E26.4.2"),sQuery(id+"F0.wireOp",EDGE,"E26.4.3"),sQuery(id+"F0.wireOp",EDGE,"E26.4.4"),sQuery(id+"F0.wireOp",EDGE,"E26.5.0"),sQuery(id+"F0.wireOp",EDGE,"E26.5.1"),sQuery(id+"F0.wireOp",EDGE,"E26.5.2"),sQuery(id+"F0.wireOp",EDGE,"E26.5.3"),sQuery(id+"F0.wireOp",EDGE,"E26.5.4"),sQuery(id+"F0.wireOp",EDGE,"E26.6.0"),sQuery(id+"F0.wireOp",EDGE,"E26.6.1"),sQuery(id+"F0.wireOp",EDGE,"E26.6.2"),sQuery(id+"F0.wireOp",EDGE,"E26.6.3"),sQuery(id+"F0.wireOp",EDGE,"E26.6.4"),sQuery(id+"F0.wireOp",EDGE,"E26.7.0"),sQuery(id+"F0.wireOp",EDGE,"E26.7.1"),sQuery(id+"F0.wireOp",EDGE,"E26.7.2"),sQuery(id+"F0.wireOp",EDGE,"E26.7.3"),sQuery(id+"F0.wireOp",EDGE,"E26.7.4"),sQuery(id+"F0.wireOp",EDGE,"E26.8.0"),sQuery(id+"F0.wireOp",EDGE,"E26.8.1"),sQuery(id+"F0.wireOp",EDGE,"E26.8.2"),sQuery(id+"F0.wireOp",EDGE,"E26.8.3"),sQuery(id+"F0.wireOp",EDGE,"E26.8.4"),sQuery(id+"F0.wireOp",EDGE,"E26.9.0"),sQuery(id+"F0.wireOp",EDGE,"E26.9.1"),sQuery(id+"F0.wireOp",EDGE,"E26.9.2"),sQuery(id+"F0.wireOp",EDGE,"E26.9.3"),sQuery(id+"F0.wireOp",EDGE,"E26.9.4"),sQuery(id+"F0.wireOp",EDGE,"E26.10.0"),sQuery(id+"F0.wireOp",EDGE,"E26.10.1"),sQuery(id+"F0.wireOp",EDGE,"E26.10.2"),sQuery(id+"F0.wireOp",EDGE,"E26.10.3"),sQuery(id+"F0.wireOp",EDGE,"E26.10.4"),sQuery(id+"F0.wireOp",EDGE,"E26.11.0"),sQuery(id+"F0.wireOp",EDGE,"E26.11.1"),sQuery(id+"F0.wireOp",EDGE,"E26.11.2"),sQuery(id+"F0.wireOp",EDGE,"E26.11.3"),sQuery(id+"F0.wireOp",EDGE,"E26.11.4"),sQuery(id+"F0.wireOp",EDGE,"E26.12.0"),sQuery(id+"F0.wireOp",EDGE,"E26.12.1"),sQuery(id+"F0.wireOp",EDGE,"E26.12.2"),sQuery(id+"F0.wireOp",EDGE,"E26.12.3"),sQuery(id+"F0.wireOp",EDGE,"E26.12.4"),sQuery(id+"F0.wireOp",EDGE,"E26.13.0"),sQuery(id+"F0.wireOp",EDGE,"E26.13.1"),sQuery(id+"F0.wireOp",EDGE,"E26.13.2"),sQuery(id+"F0.wireOp",EDGE,"E26.13.3"),sQuery(id+"F0.wireOp",EDGE,"E26.13.4"),sQuery(id+"F0.wireOp",EDGE,"E26.14.0"),sQuery(id+"F0.wireOp",EDGE,"E26.14.1"),sQuery(id+"F0.wireOp",EDGE,"E26.14.2"),sQuery(id+"F0.wireOp",EDGE,"E26.14.3"),sQuery(id+"F0.wireOp",EDGE,"E26.14.4"),sQuery(id+"F0.wireOp",EDGE,"E26.15.0"),sQuery(id+"F0.wireOp",EDGE,"E26.15.1"),sQuery(id+"F0.wireOp",EDGE,"E26.15.2"),sQuery(id+"F0.wireOp",EDGE,"E26.15.3"),sQuery(id+"F0.wireOp",EDGE,"E26.15.4"),sQuery(id+"F0.wireOp",EDGE,"E26.16.0"),sQuery(id+"F0.wireOp",EDGE,"E26.16.1"),sQuery(id+"F0.wireOp",EDGE,"E26.16.2"),sQuery(id+"F0.wireOp",EDGE,"E26.16.3"),sQuery(id+"F0.wireOp",EDGE,"E26.16.4"),sQuery(id+"F0.wireOp",EDGE,"E26.17.0"),sQuery(id+"F0.wireOp",EDGE,"E26.17.1"),sQuery(id+"F0.wireOp",EDGE,"E26.17.2"),sQuery(id+"F0.wireOp",EDGE,"E26.17.3"),sQuery(id+"F0.wireOp",EDGE,"E26.17.4"),sQuery(id+"F0.wireOp",EDGE,"E26.18.0"),sQuery(id+"F0.wireOp",EDGE,"E26.18.1"),sQuery(id+"F0.wireOp",EDGE,"E26.18.2"),sQuery(id+"F0.wireOp",EDGE,"E26.18.3"),sQuery(id+"F0.wireOp",EDGE,"E26.18.4"),sQuery(id+"F0.wireOp",EDGE,"E26.19.0"),sQuery(id+"F0.wireOp",EDGE,"E26.19.1"),sQuery(id+"F0.wireOp",EDGE,"E26.19.2"),sQuery(id+"F0.wireOp",EDGE,"E26.19.3"),sQuery(id+"F0.wireOp",EDGE,"E26.19.4"),sQuery(id+"F0.wireOp",EDGE,"E27.trimOffspring"),sQuery(id+"F0.wireOp",EDGE,"E28.trimOffspring"),sQuery(id+"F0.wireOp",EDGE,"E29.trimOffspring"),sQuery(id+"F0.wireOp",EDGE,"E30.trimOffspring"),sQuery(id+"F0.wireOp",EDGE,"E31.trimOffspring"),sQuery(id+"F0.wireOp",EDGE,"E32.trimOffspring"),sQuery(id+"F0.wireOp",EDGE,"E33.trimOffspring"),sQuery(id+"F0.wireOp",EDGE,"E34.trimOffspring"),sQuery(id+"F0.wireOp",EDGE,"E35.trimOffspring"),sQuery(id+"F0.wireOp",EDGE,"E36.trimOffspring"),sQuery(id+"F0.wireOp",EDGE,"E37.trimOffspring"),sQuery(id+"F0.wireOp",EDGE,"E38.trimOffspring"),sQuery(id+"F0.wireOp",EDGE,"E39.trimOffspring"),sQuery(id+"F0.wireOp",EDGE,"E40.trimOffspring"),sQuery(id+"F0.wireOp",EDGE,"E41.trimOffspring"),sQuery(id+"F0.wireOp",EDGE,"E42.trimOffspring"),sQuery(id+"F0.wireOp",EDGE,"E43.trimOffspring"),sQuery(id+"F0.wireOp",EDGE,"E44.trimOffspring"),sQuery(id+"F0.wireOp",EDGE,"E45.trimOffspring")])],"isStart":true}),makeQuery(id+"F5.opExtrude","SWEPT_FACE",FACE,{"disambiguationData":[OSD([sQuery(id+"F4.wireOp",EDGE,"E55")])]})]});
            chamfer(context, id + "F7", {"entities" : qUnion([Q0]), "width" : 2 * mm, "tangentPropagation" : true});
        }
    });
